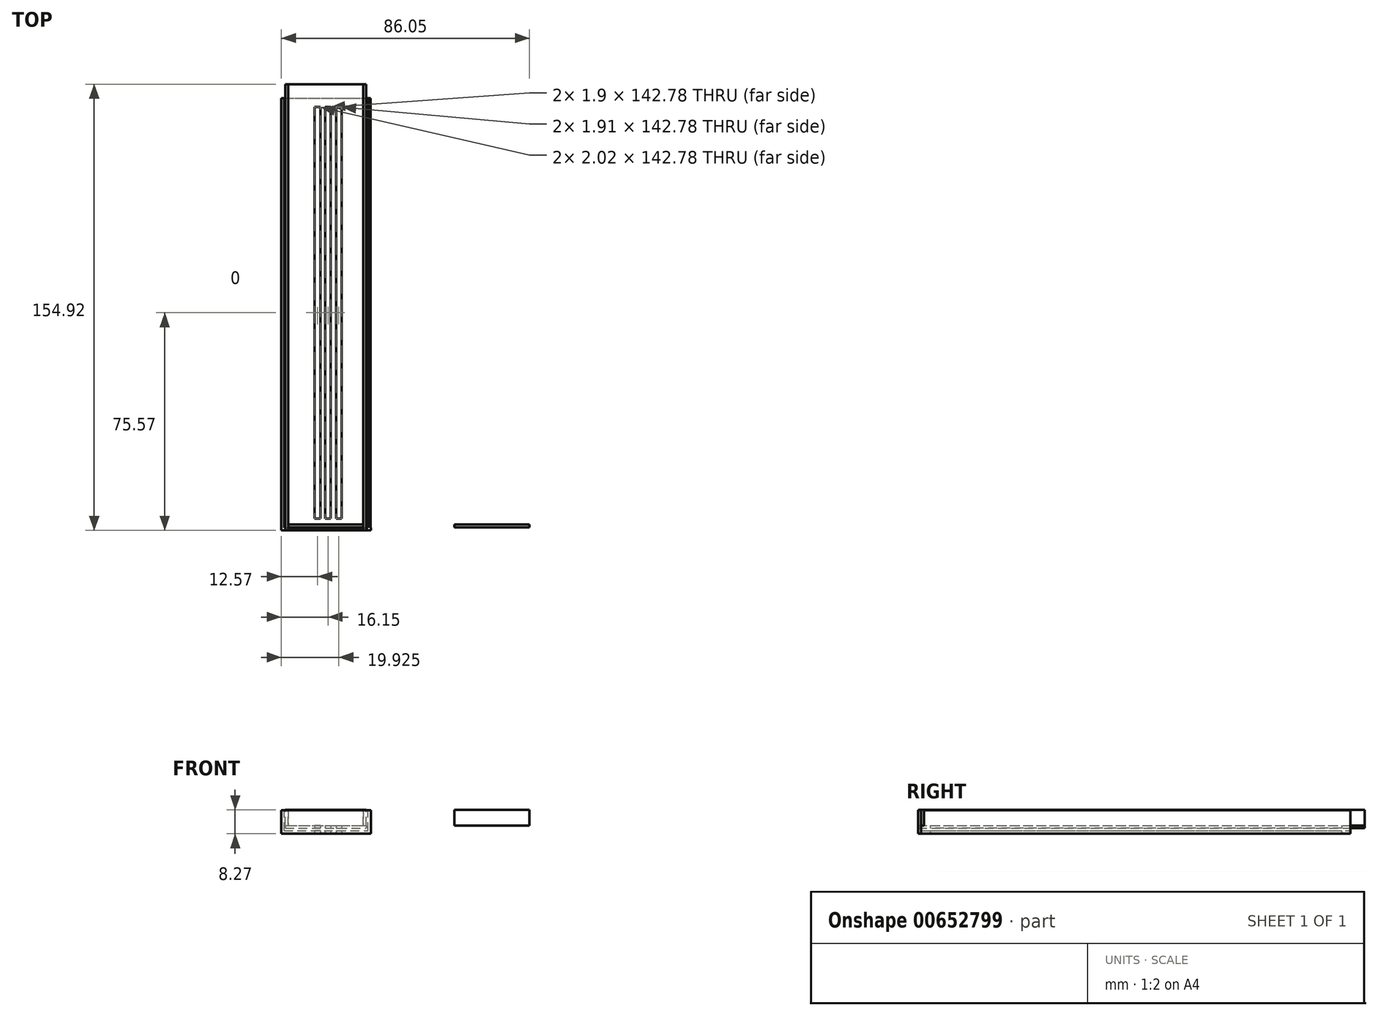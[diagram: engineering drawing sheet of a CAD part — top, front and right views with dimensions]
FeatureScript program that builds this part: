
annotation { "Feature Type Name" : "Feature", "Feature Type Description" : "" }
export const myFeature = defineFeature(function(context is Context, id is Id, definition is map)
    precondition{}
    {
        {
            var Q0;
            Q0=qCreatedBy(makeId("Top.planeOp"),FACE);
            var sketch = newSketch(context, id + "F0", { "sketchPlane" : qUnion([Q0])});
            skLineSegment(sketch, "E0.bottom", {"start": v(-52.3, 55.12) * mm, "end": v(-22.3, 55.12) * mm});
            skLineSegment(sketch, "E0.top", {"start": v(-52.3, -94.88) * mm, "end": v(-22.3, -94.88) * mm});
            skLineSegment(sketch, "E0.left", {"start": v(-52.3, 55.12) * mm, "end": v(-52.3, -94.88) * mm});
            skLineSegment(sketch, "E0.right", {"start": v(-22.3, 55.12) * mm, "end": v(-22.3, -94.88) * mm});
            skSolve(sketch);
        }
        {
            var Q0;
            Q0 = qSketchRegion(id + "F0", true);
            extrude(context, id + "F1", {"entities" : qUnion([Q0]), "depth" : 1 * mm, "offsetDistance" : 25 * mm});
        }
        {
            var Q0;
            Q0=makeQuery(id+"F1.opExtrude","SWEPT_FACE",FACE,{"disambiguationData":[OSD([sQuery(id+"F0.wireOp",EDGE,"E0.right")])]});
            var sketch = newSketch(context, id + "F2", { "sketchPlane" : qUnion([Q0])});
            skLineSegment(sketch, "E1.bottom", {"start": v(55.12, 0) * mm, "end": v(-94.87, 0) * mm});
            skLineSegment(sketch, "E1.top", {"start": v(55.12, 8.22) * mm, "end": v(-94.87, 8.22) * mm});
            skLineSegment(sketch, "E1.left", {"start": v(55.12, 0) * mm, "end": v(55.12, 8.22) * mm});
            skLineSegment(sketch, "E1.right", {"start": v(-94.87, 0) * mm, "end": v(-94.87, 8.22) * mm});
            skSolve(sketch);
        }
        {
            var Q0;
            Q0 = qSketchRegion(id + "F2", true);
            extrude(context, id + "F3", {"entities" : qUnion([Q0]), "depth" : 1 * mm, "offsetDistance" : 25 * mm});
        }
        {
            var Q0;
            Q0=makeQuery(id+"F3.opExtrude","SWEPT_BODY",BODY,{"disambiguationData":[OSD([sQuery(id+"F2.wireOp",EDGE,"E1.bottom"),sQuery(id+"F2.wireOp",EDGE,"E1.top"),sQuery(id+"F2.wireOp",EDGE,"E1.left"),sQuery(id+"F2.wireOp",EDGE,"E1.right")])]});
            transform(context, id + "F4", {"entities" : qUnion([Q0]), "transformType" : TransformType.TRANSLATION_3D, "dx" : -30 * mm, "dy" : 0 * mm, "dz" : 0 * mm, "makeCopy" : true});
        }
        {
            var Q0;
            Q0=makeQuery(id+"F1.opExtrude","SWEPT_FACE",FACE,{"disambiguationData":[OSD([sQuery(id+"F0.wireOp",EDGE,"E0.top")])]});
            var sketch = newSketch(context, id + "F5", { "sketchPlane" : qUnion([Q0])});
            skLineSegment(sketch, "E2.bottom", {"start": v(-52.3, 0) * mm, "end": v(-21.28, 0) * mm});
            skLineSegment(sketch, "E2.top", {"start": v(-52.3, 8.22) * mm, "end": v(-21.28, 8.22) * mm});
            skLineSegment(sketch, "E2.left", {"start": v(-52.3, 0) * mm, "end": v(-52.3, 8.22) * mm});
            skLineSegment(sketch, "E2.right", {"start": v(-21.28, 0) * mm, "end": v(-21.28, 8.22) * mm});
            skSolve(sketch);
        }
        {
            var Q0;
            Q0 = qSketchRegion(id + "F5", true);
            extrude(context, id + "F6", {"entities" : qUnion([Q0]), "operationType" : NewBodyOperationType.ADD, "depth" : -1 * mm, "offsetDistance" : 25 * mm});
        }
        {
            var Q0;
            Q0=qCreatedBy(makeId("Top.planeOp"),FACE);
            var sketch = newSketch(context, id + "F7", { "sketchPlane" : qUnion([Q0])});
            skLineSegment(sketch, "E3.bottom", {"start": v(-51.41, -94.84) * mm, "end": v(-23.36, -94.84) * mm});
            skLineSegment(sketch, "E3.top", {"start": v(-51.41, 60.04) * mm, "end": v(-23.36, 60.04) * mm});
            skLineSegment(sketch, "E3.left", {"start": v(-51.41, -94.84) * mm, "end": v(-51.41, 60.04) * mm});
            skLineSegment(sketch, "E3.right", {"start": v(-23.36, -94.84) * mm, "end": v(-23.36, 60.04) * mm});
            skSolve(sketch);
        }
        {
            var Q0;
            Q0 = qSketchRegion(id + "F7", true);
            extrude(context, id + "F8", {"entities" : qUnion([Q0]), "depth" : 1 * mm, "offsetDistance" : 25 * mm});
        }
        {
            var Q0;
            Q0=makeQuery(id+"F8.opExtrude","SWEPT_BODY",BODY,{"disambiguationData":[OSD([sQuery(id+"F7.wireOp",EDGE,"E3.bottom"),sQuery(id+"F7.wireOp",EDGE,"E3.top"),sQuery(id+"F7.wireOp",EDGE,"E3.left"),sQuery(id+"F7.wireOp",EDGE,"E3.right")])]});
            transform(context, id + "F9", {"entities" : qUnion([Q0]), "transformType" : TransformType.TRANSLATION_3D, "dx" : 0.5 * mm, "dy" : 0 * mm, "dz" : 1.9 * mm, "makeCopy" : false});
        }
        {
            var Q0;
            Q0=makeQuery(id+"F8.opExtrude","SWEPT_FACE",FACE,{"disambiguationData":[OSD([sQuery(id+"F7.wireOp",EDGE,"E3.right")])]});
            var sketch = newSketch(context, id + "F10", { "sketchPlane" : qUnion([Q0])});
            skLineSegment(sketch, "E4.bottom", {"start": v(60.04, 2.9) * mm, "end": v(-94.84, 2.9) * mm});
            skLineSegment(sketch, "E4.top", {"start": v(60.04, 8.24) * mm, "end": v(-94.84, 8.24) * mm});
            skLineSegment(sketch, "E4.left", {"start": v(60.04, 2.9) * mm, "end": v(60.04, 8.24) * mm});
            skLineSegment(sketch, "E4.right", {"start": v(-94.84, 2.9) * mm, "end": v(-94.84, 8.24) * mm});
            skSolve(sketch);
        }
        {
            var Q0;
            Q0 = qSketchRegion(id + "F10", true);
            extrude(context, id + "F11", {"entities" : qUnion([Q0]), "depth" : -1 * mm, "offsetDistance" : 25 * mm});
        }
        {
            var Q0;
            Q0=makeQuery(id+"F11.opExtrude","SWEPT_BODY",BODY,{"disambiguationData":[OSD([sQuery(id+"F10.wireOp",EDGE,"E4.bottom"),sQuery(id+"F10.wireOp",EDGE,"E4.top"),sQuery(id+"F10.wireOp",EDGE,"E4.left"),sQuery(id+"F10.wireOp",EDGE,"E4.right")])]});
            transform(context, id + "F12", {"entities" : qUnion([Q0]), "transformType" : TransformType.TRANSLATION_3D, "dx" : -27.06 * mm, "dy" : 0 * mm, "dz" : 0 * mm, "makeCopy" : true});
        }
        {
            var Q0;
            Q0=makeQuery(id+"F8.opExtrude","SWEPT_FACE",FACE,{"disambiguationData":[OSD([sQuery(id+"F7.wireOp",EDGE,"E3.top")])]});
            var sketch = newSketch(context, id + "F13", { "sketchPlane" : qUnion([Q0])});
            skLineSegment(sketch, "E5.bottom", {"start": v(49.88, 8.27) * mm, "end": v(23.85, 8.27) * mm});
            skLineSegment(sketch, "E5.top", {"start": v(49.88, 2.9) * mm, "end": v(23.85, 2.9) * mm});
            skLineSegment(sketch, "E5.left", {"start": v(49.88, 8.27) * mm, "end": v(49.88, 2.9) * mm});
            skLineSegment(sketch, "E5.right", {"start": v(23.85, 8.27) * mm, "end": v(23.85, 2.9) * mm});
            skSolve(sketch);
        }
        {
            var Q0;
            Q0=makeQuery(id+"F13.imprint","IMPRINT",FACE,{"disambiguationData":[TD([[makeQuery(id+"F13.imprint","IMPRINT",EDGE,{"derivedFrom":sQuery(id+"F13.wireOp",EDGE,"E5.bottom")}),1.0]])]});
            extrude(context, id + "F14", {"entities" : qUnion([Q0]), "depth" : -1 * mm, "offsetDistance" : 25 * mm});
        }
        {
            var Q0;
            Q0=makeQuery(id+"F14.opExtrude","SWEPT_BODY",BODY,{"disambiguationData":[OSD([sQuery(id+"F13.wireOp",EDGE,"E5.bottom"),sQuery(id+"F13.wireOp",EDGE,"E5.top"),sQuery(id+"F13.wireOp",EDGE,"E5.left"),sQuery(id+"F13.wireOp",EDGE,"E5.right")])]});
            transform(context, id + "F15", {"entities" : qUnion([Q0]), "transformType" : TransformType.TRANSLATION_3D, "dx" : 0 * mm, "dy" : -153.89 * mm, "dz" : 0 * mm, "makeCopy" : false});
        }
        {
            var Q0;
            Q0=makeQuery(id+"F6.boolean.opBoolean","MERGE",FACE,{"derivedFrom":[makeQuery(id+"F1.opExtrude","CAP_FACE",FACE,{"disambiguationData":[OSD([sQuery(id+"F0.wireOp",EDGE,"E0.bottom"),sQuery(id+"F0.wireOp",EDGE,"E0.top"),sQuery(id+"F0.wireOp",EDGE,"E0.left"),sQuery(id+"F0.wireOp",EDGE,"E0.right")])],"isStart":true}),makeQuery(id+"F6.opExtrude","SWEPT_FACE",FACE,{"disambiguationData":[OSD([sQuery(id+"F5.wireOp",EDGE,"E2.bottom")])]})]});
            var sketch = newSketch(context, id + "F16", { "sketchPlane" : qUnion([Q0])});
            skLineSegment(sketch, "E6.bottom", {"start": v(-40.74, 90.7) * mm, "end": v(-31.42, 90.7) * mm, "construction": true});
            skLineSegment(sketch, "E6.top", {"start": v(-40.74, -52.08) * mm, "end": v(-31.42, -52.08) * mm, "construction": true});
            skLineSegment(sketch, "E6.left", {"start": v(-40.74, 90.7) * mm, "end": v(-40.74, -52.08) * mm, "construction": true});
            skLineSegment(sketch, "E6.right", {"start": v(-31.42, 90.7) * mm, "end": v(-31.42, -52.08) * mm, "construction": true});
            skLineSegment(sketch, "E7.bottom", {"start": v(-41.3, 90.7) * mm, "end": v(-33.84, 90.7) * mm, "construction": true});
            skLineSegment(sketch, "E7.top", {"start": v(-41.3, -55.12) * mm, "end": v(-33.84, -55.12) * mm, "construction": true});
            skLineSegment(sketch, "E7.left", {"start": v(-41.3, 90.7) * mm, "end": v(-41.3, -55.12) * mm, "construction": true});
            skLineSegment(sketch, "E7.right", {"start": v(-33.84, 90.7) * mm, "end": v(-33.84, -55.12) * mm, "construction": true});
            skLineSegment(sketch, "E8.bottom", {"start": v(-40.74, -52.08) * mm, "end": v(-38.72, -52.08) * mm});
            skLineSegment(sketch, "E8.top", {"start": v(-40.74, 90.7) * mm, "end": v(-38.72, 90.7) * mm});
            skLineSegment(sketch, "E8.left", {"start": v(-40.74, -52.08) * mm, "end": v(-40.74, 90.7) * mm});
            skLineSegment(sketch, "E8.right", {"start": v(-38.72, -52.08) * mm, "end": v(-38.72, 90.7) * mm});
            skLineSegment(sketch, "E9.bottom", {"start": v(-31.42, 90.7) * mm, "end": v(-33.33, 90.7) * mm});
            skLineSegment(sketch, "E9.top", {"start": v(-31.42, -52.08) * mm, "end": v(-33.33, -52.08) * mm});
            skLineSegment(sketch, "E9.left", {"start": v(-31.42, 90.7) * mm, "end": v(-31.42, -52.08) * mm});
            skLineSegment(sketch, "E9.right", {"start": v(-33.33, 90.7) * mm, "end": v(-33.33, -52.08) * mm});
            skLineSegment(sketch, "E10.bottom", {"start": v(-35.2, -52.08) * mm, "end": v(-37.1, -52.08) * mm});
            skLineSegment(sketch, "E10.top", {"start": v(-35.2, 90.7) * mm, "end": v(-37.1, 90.7) * mm});
            skLineSegment(sketch, "E10.left", {"start": v(-35.2, -52.08) * mm, "end": v(-35.2, 90.7) * mm});
            skLineSegment(sketch, "E10.right", {"start": v(-37.1, -52.08) * mm, "end": v(-37.1, 90.7) * mm});
            skSolve(sketch);
        }
        {
            var Q0;
            Q0 = qSketchRegion(id + "F16", true);
            extrude(context, id + "F17", {"entities" : qUnion([Q0]), "operationType" : NewBodyOperationType.REMOVE, "oppositeDirection" : true, "depth" : 25 * mm, "offsetDistance" : 25 * mm});
        }
        {
            var Q0;
            Q0=makeQuery(id+"F14.opExtrude","SWEPT_BODY",BODY,{"disambiguationData":[OSD([sQuery(id+"F13.wireOp",EDGE,"E5.bottom"),sQuery(id+"F13.wireOp",EDGE,"E5.top"),sQuery(id+"F13.wireOp",EDGE,"E5.left"),sQuery(id+"F13.wireOp",EDGE,"E5.right")])]});
            transform(context, id + "F18", {"entities" : qUnion([Q0]), "transformType" : TransformType.TRANSLATION_3D, "dx" : 0 * mm, "dy" : 1 * mm, "dz" : 0 * mm, "makeCopy" : false});
        }
        {
            var Q0;
            Q0=makeQuery(id+"F14.opExtrude","SWEPT_BODY",BODY,{"disambiguationData":[OSD([sQuery(id+"F13.wireOp",EDGE,"E5.bottom"),sQuery(id+"F13.wireOp",EDGE,"E5.top"),sQuery(id+"F13.wireOp",EDGE,"E5.left"),sQuery(id+"F13.wireOp",EDGE,"E5.right")])]});
            transform(context, id + "F19", {"entities" : qUnion([Q0]), "transformType" : TransformType.TRANSLATION_3D, "dx" : 57.6 * mm, "dy" : 0 * mm, "dz" : 0 * mm, "makeCopy" : true});
        }
    });
